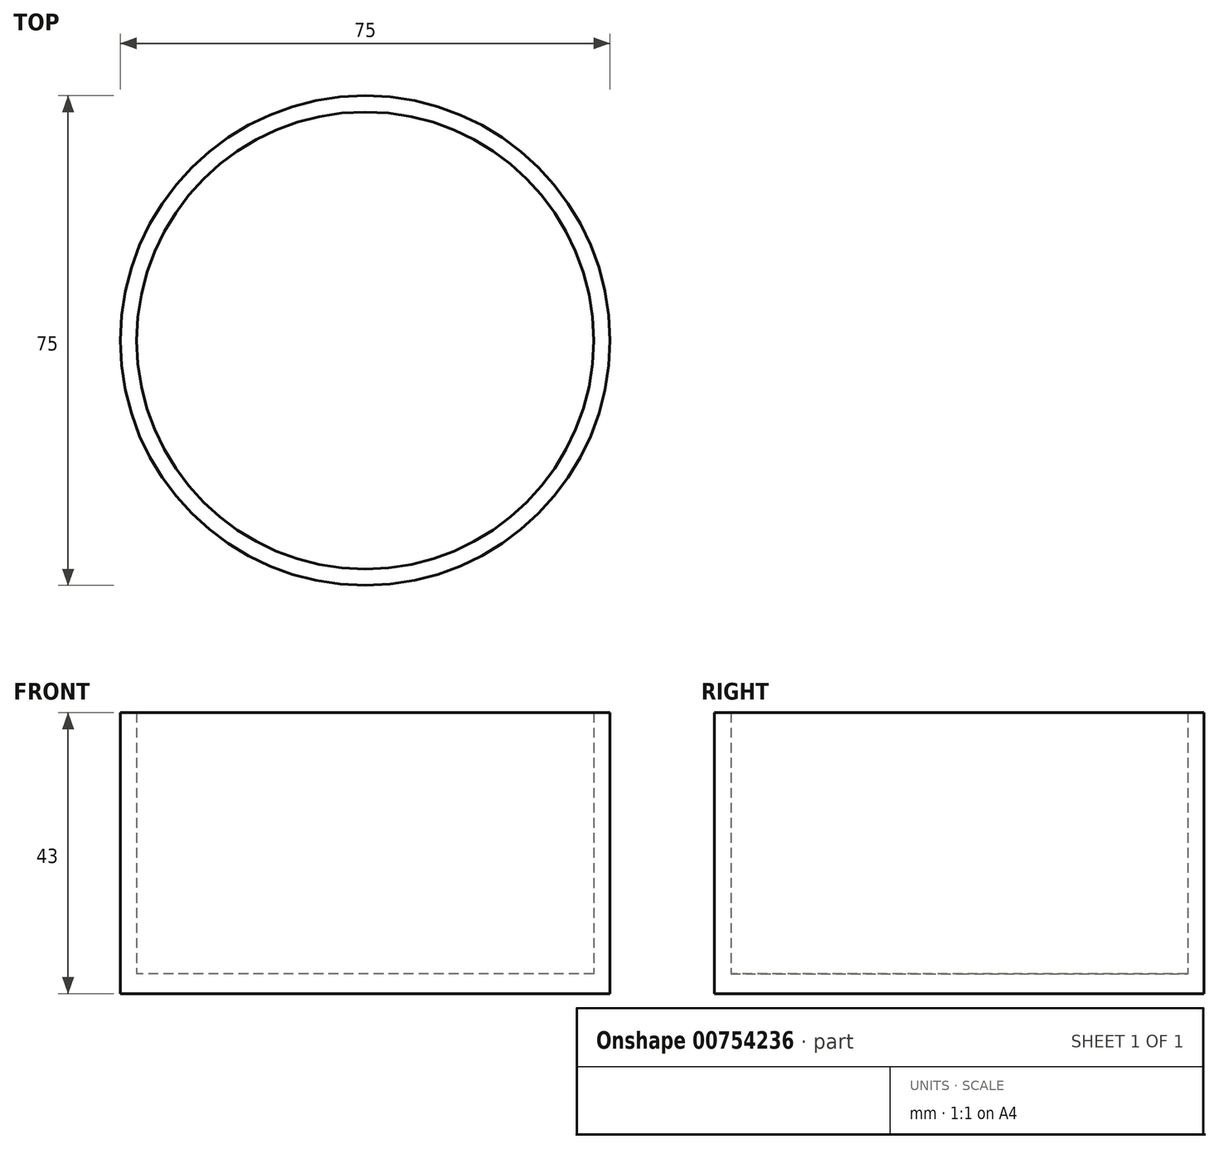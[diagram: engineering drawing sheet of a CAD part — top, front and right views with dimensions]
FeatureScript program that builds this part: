
annotation { "Feature Type Name" : "Feature", "Feature Type Description" : "" }
export const myFeature = defineFeature(function(context is Context, id is Id, definition is map)
    precondition{}
    {
        {
            var Q0;
            Q0=qCreatedBy(makeId("Top.planeOp"),FACE);
            var sketch = newSketch(context, id + "F0", { "sketchPlane" : qUnion([Q0])});
            skCircle(sketch, "E0", {"center": v(0, 0) * mm, "radius": 37.5 * mm});
            skSolve(sketch);
        }
        {
            var Q0;
            Q0 = qSketchRegion(id + "F0", true);
            extrude(context, id + "F1", {"entities" : qUnion([Q0]), "depth" : 3 * mm, "offsetDistance" : 25 * mm});
        }
        {
            var Q0;
            Q0=makeQuery(id+"F1.opExtrude","CAP_FACE",FACE,{"disambiguationData":[OSD([sQuery(id+"F0.wireOp",EDGE,"E0")])],"isStart":false});
            var sketch = newSketch(context, id + "F2", { "sketchPlane" : qUnion([Q0])});
            skCircle(sketch, "E1", {"center": v(0, 0) * mm, "radius": 35 * mm});
            skCircle(sketch, "E2.0", {"center": v(0, 0) * mm, "radius": 37.5 * mm});
            skSolve(sketch);
        }
        {
            var Q0;
            Q0=makeQuery(id+"F2.imprint","IMPRINT",FACE,{"disambiguationData":[TD([[makeQuery(id+"F2.imprint","IMPRINT",EDGE,{"derivedFrom":sQuery(id+"F2.wireOp",EDGE,"E1")}),-1.0]])]});
            extrude(context, id + "F3", {"entities" : qUnion([Q0]), "operationType" : NewBodyOperationType.ADD, "depth" : 40 * mm, "offsetDistance" : 25 * mm});
        }
    });
